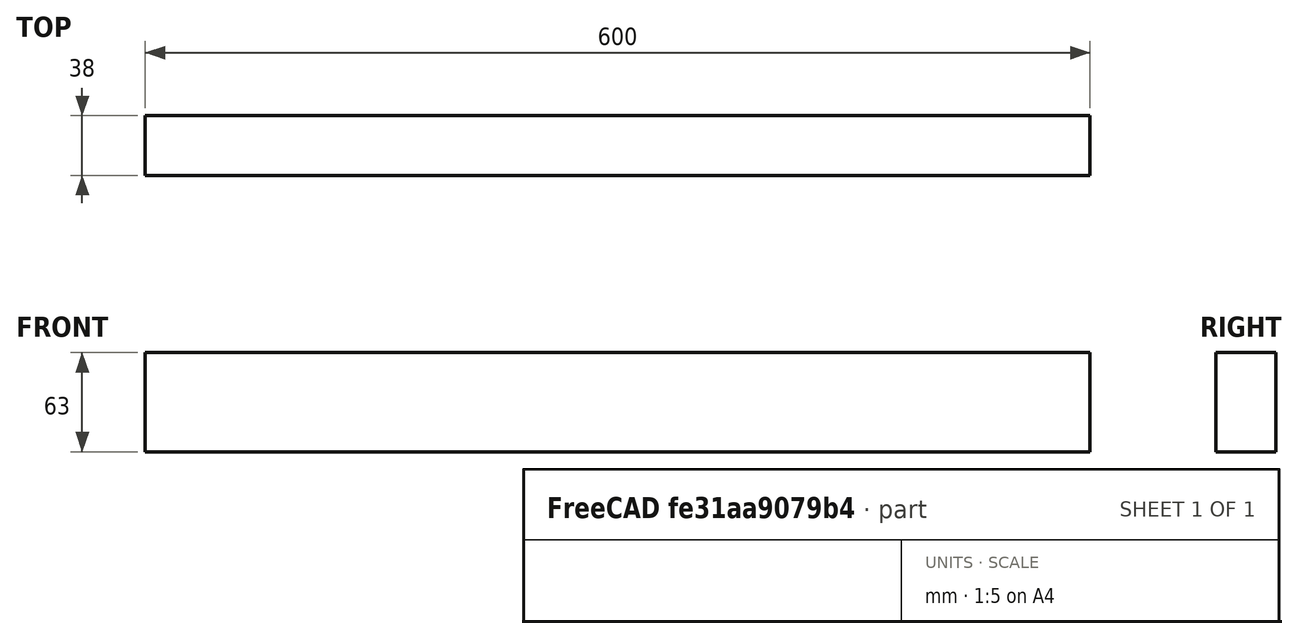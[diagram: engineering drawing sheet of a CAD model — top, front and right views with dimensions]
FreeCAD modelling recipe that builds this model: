
FCSTD DOCUMENT  (FreeCAD 0.21R33771 (Git))
Label: reflector_2024_timber_half
License: All rights reserved
LicenseURL: https://en.wikipedia.org/wiki/All_rights_reserved
objects: Spreadsheet::Sheet×1, Sketcher::SketchObject×1, PartDesign::Pad×1, PartDesign::Body×1
note: 4 computed .brp shape members not serialized (recipe doc carries the construction recipe); baked Part::Feature solids carry a one-line shape summary decoded from their .brp

FEATURE [Spreadsheet::Sheet] Spreadsheet  label="d"
  cells = A1='width; B1(width)=38; A2='height; B2(height)=63; A3='length; B3(length)=600
FEATURE [Sketcher::SketchObject] Sketch
  FullyConstrained = true
  MapMode = 5
  Placement = pos=(0,0,0) rot=(0.57735,0.57735,0.57735;2.0944rad)
  Support = -> [YZ_Plane]
  expr: Constraints[5] = <<d>>.width
  expr: Constraints[6] = <<d>>.height
  sketch-geometry (4):
    g0: LineSegment StartX=-19 StartY=31.5 StartZ=0 EndX=19 EndY=31.5 EndZ=0
    g1: LineSegment StartX=19 StartY=31.5 StartZ=0 EndX=19 EndY=-31.5 EndZ=0
    g2: LineSegment StartX=19 StartY=-31.5 StartZ=0 EndX=-19 EndY=-31.5 EndZ=0
    g3: LineSegment StartX=-19 StartY=-31.5 StartZ=0 EndX=-19 EndY=31.5 EndZ=0
  constraints (10):
    c: Coincident(g0,g1)
    c: Coincident(g1,g2)
    c: Coincident(g2,g3)
    c: Coincident(g3,g0)
    c: Horizontal(g2)
    c: DistanceX(g0,g0) = 38
    c: DistanceY(g3,g3) = 63
    c: Symmetric(g0,g0,g-2)
    c: Symmetric(g0,g1,g-1)
    c: Vertical(g3)
FEATURE [PartDesign::Pad] Pad
  Direction = (1,-2e-16,3e-16)
  Length = 600
  Length2 = 10
  Midplane = true
  Placement = pos=(0,0,0) rot=(0.57735,0.57735,0.57735;2.0944rad)
  Profile = -> Sketch
  ReferenceAxis = -> Sketch [N_Axis]
  Type = 0
  expr: Length = <<d>>.length
FEATURE [PartDesign::Body] Body  label="timber_batten_600"
  Group = -> [Sketch,Pad]
  Origin = -> Origin
  Tip = -> Pad
